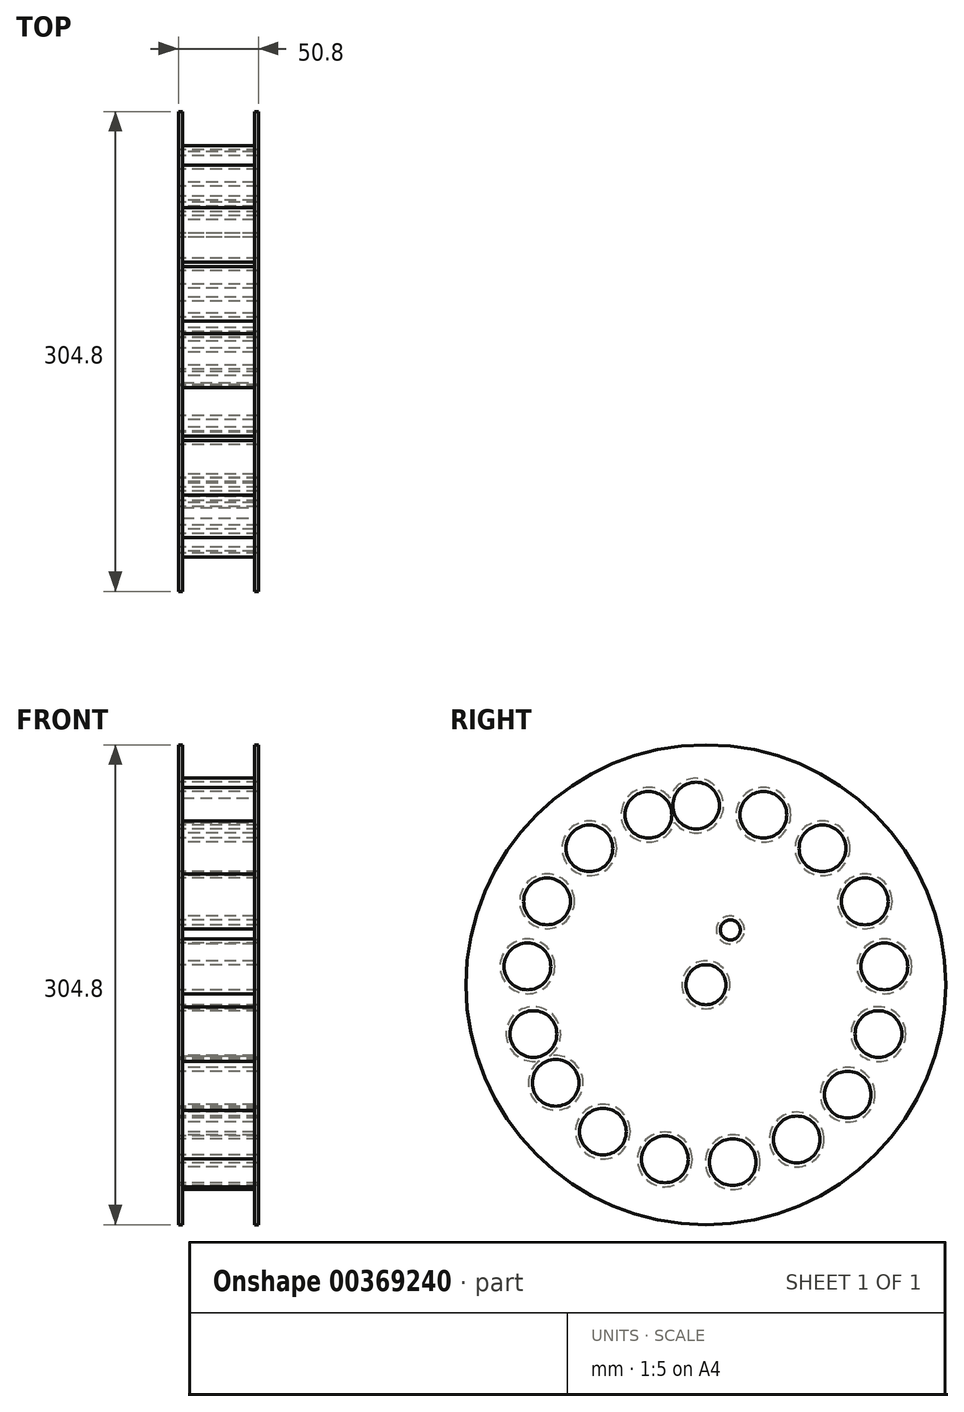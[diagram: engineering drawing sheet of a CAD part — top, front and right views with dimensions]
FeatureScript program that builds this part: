
annotation { "Feature Type Name" : "Feature", "Feature Type Description" : "" }
export const myFeature = defineFeature(function(context is Context, id is Id, definition is map)
    precondition{}
    {
        {
            var Q0;
            Q0=qCreatedBy(makeId("Right.planeOp"),FACE);
            var sketch = newSketch(context, id + "F0", { "sketchPlane" : qUnion([Q0])});
            skCircle(sketch, "E0", {"center": v(0, 0) * mm, "radius": 152.4 * mm});
            skCircle(sketch, "E1", {"center": v(-6.23, 113.79) * mm, "radius": 14.84 * mm});
            skCircle(sketch, "E2.1.0", {"center": v(36.5, 107.95) * mm, "radius": 14.84 * mm});
            skCircle(sketch, "E2.2.0", {"center": v(74.01, 86.65) * mm, "radius": 14.84 * mm});
            skLineSegment(sketch, "E2.anchor1", {"start": v(0, 0) * mm, "end": v(-6.23, 113.79) * mm, "construction": true});
            skLineSegment(sketch, "E2.anchor2", {"start": v(0, 0) * mm, "end": v(-95.43, -62.29) * mm, "construction": true});
            skCircle(sketch, "E3.1.3.0", {"center": v(100.92, 52.93) * mm, "radius": 14.84 * mm});
            skCircle(sketch, "E3.1.4.0", {"center": v(113.36, 11.64) * mm, "radius": 14.84 * mm});
            skCircle(sketch, "E3.1.5.0", {"center": v(109.57, -31.33) * mm, "radius": 14.84 * mm});
            skCircle(sketch, "E3.1.6.0", {"center": v(90.07, -69.8) * mm, "radius": 14.84 * mm});
            skCircle(sketch, "E3.1.7.0", {"center": v(57.68, -98.28) * mm, "radius": 14.84 * mm});
            skCircle(sketch, "E3.1.8.0", {"center": v(17.02, -112.68) * mm, "radius": 14.84 * mm});
            skCircle(sketch, "E3.1.9.0", {"center": v(-26.08, -110.93) * mm, "radius": 14.84 * mm});
            skCircle(sketch, "E3.1.10.0", {"center": v(-65.44, -93.3) * mm, "radius": 14.84 * mm});
            skCircle(sketch, "E3.1.11.0", {"center": v(-95.43, -62.29) * mm, "radius": 14.84 * mm});
            skCircle(sketch, "E4.MirrorC", {"center": v(-74.01, 86.65) * mm, "radius": 14.84 * mm});
            skCircle(sketch, "E5.MirrorC", {"center": v(-100.92, 52.93) * mm, "radius": 14.84 * mm});
            skCircle(sketch, "E6.MirrorC", {"center": v(-113.36, 11.64) * mm, "radius": 14.84 * mm});
            skCircle(sketch, "E7.MirrorC", {"center": v(-109.57, -31.33) * mm, "radius": 14.84 * mm});
            skCircle(sketch, "E8.MirrorC", {"center": v(-36.5, 107.95) * mm, "radius": 14.84 * mm});
            skCircle(sketch, "E9", {"center": v(0, 0) * mm, "radius": 12.7 * mm});
            skCircle(sketch, "E10", {"center": v(15.51, 34.8) * mm, "radius": 6.35 * mm});
            skSolve(sketch);
        }
        {
            var Q0;
            Q0 = qSketchRegion(id + "F0", true);
            extrude(context, id + "F1", {"entities" : qUnion([Q0]), "depth" : 50.8 * mm});
        }
        {
            var Q0;
            Q0=makeQuery(id+"F1.opExtrude","SWEPT_FACE",FACE,{"disambiguationData":[OSD([sQuery(id+"F0.wireOp",EDGE,"E0")])]});
            shell(context, id + "F2", {"entities" : qUnion([Q0]), "thickness" : 2.54 * mm});
        }
    });
